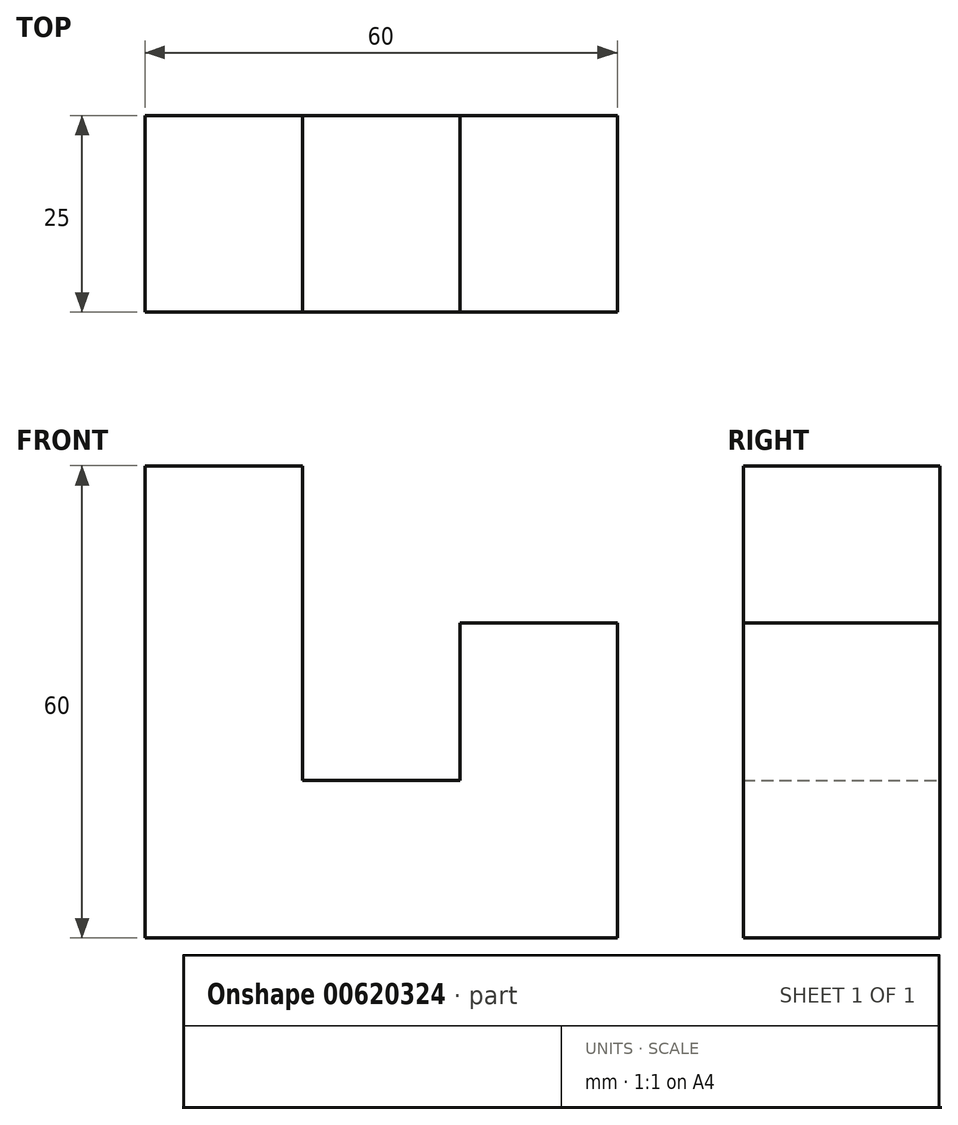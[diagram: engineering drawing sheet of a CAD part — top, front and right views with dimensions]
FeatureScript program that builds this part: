
annotation { "Feature Type Name" : "Feature", "Feature Type Description" : "" }
export const myFeature = defineFeature(function(context is Context, id is Id, definition is map)
    precondition{}
    {
        {
            var Q0;
            Q0=qCreatedBy(makeId("Front.planeOp"),FACE);
            var sketch = newSketch(context, id + "F0", { "sketchPlane" : qUnion([Q0])});
            skLineSegment(sketch, "E0", {"start": v(-74.34, 57.69) * mm, "end": v(-74.34, -2.31) * mm});
            skLineSegment(sketch, "E1", {"start": v(-74.34, -2.31) * mm, "end": v(-14.34, -2.31) * mm});
            skLineSegment(sketch, "E2", {"start": v(-14.34, -2.31) * mm, "end": v(-14.34, 37.69) * mm});
            skLineSegment(sketch, "E3", {"start": v(-14.34, 37.69) * mm, "end": v(-34.34, 37.69) * mm});
            skLineSegment(sketch, "E4", {"start": v(-34.34, 37.69) * mm, "end": v(-34.34, 17.69) * mm});
            skLineSegment(sketch, "E5", {"start": v(-34.34, 17.69) * mm, "end": v(-54.34, 17.69) * mm});
            skLineSegment(sketch, "E6", {"start": v(-54.34, 17.69) * mm, "end": v(-54.34, 57.69) * mm});
            skLineSegment(sketch, "E7", {"start": v(-54.34, 57.69) * mm, "end": v(-74.34, 57.69) * mm});
            skSolve(sketch);
        }
        {
            var Q0;
            Q0 = qSketchRegion(id + "F0", true);
            extrude(context, id + "F1", {"entities" : qUnion([Q0]), "depth" : 25 * mm, "offsetDistance" : 25 * mm});
        }
    });
